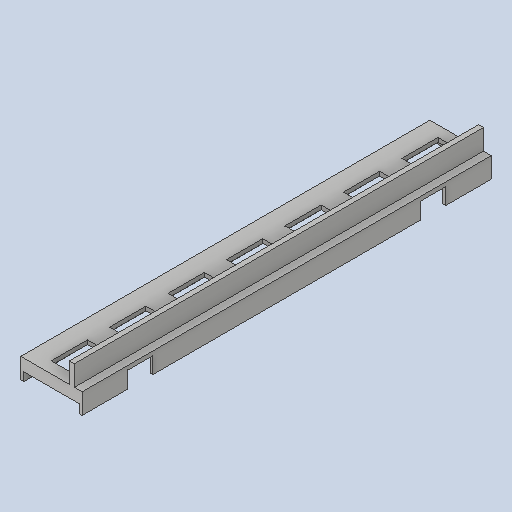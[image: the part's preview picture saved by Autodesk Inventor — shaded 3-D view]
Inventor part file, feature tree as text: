
AUTODESK INVENTOR PART (.ipt)
format: ipt  version: 2023 (Build 270158000, 158)  size: 224,768 bytes
history: native  units: mm
features: other x56, extrude x11, sketch x11
ambient origin geometry x8: Origin, YZ Plane, XZ Plane, XY Plane, X Axis, Y Axis, Z Axis, Center Point
bodies: Solid1 (feature_tree)
feature tree (78):
  extrude  "Extrusion1"  Depth=250.0mm TaperAngle=0.0deg
  extrude  "Extrusion2"  Depth=8.0mm TaperAngle=0.0deg
  extrude  "Extrusion3"  Depth=8.0mm TaperAngle=0.0deg
  extrude  "Extrusion4"  Depth=8.0mm TaperAngle=0.0deg
  extrude  "Extrusion5"  Depth=37.5mm TaperAngle=0.0deg
  extrude  "Extrusion6"  TaperAngle=0.0deg  [1 undecoded]
  extrude  "Extrusion7"  [1 undecoded]
  extrude  "Extrusion8"  [1 undecoded]
  extrude  "Extrusion9"  [1 undecoded]
  extrude  "Extrusion10"  [1 undecoded]
  extrude  "Extrusion11"  [1 undecoded]
  other  "p_XY"
  other  "p_YZ"
  other  "p_ZX"
  other  "p_X"
  other  "p_Y"
  other  "p_Z"
  other  "p_Center"
  other  "p1_XY"
  other  "p1_YZ"
  other  "p1_ZX"
  other  "p1_X"
  other  "p1_Y"
  other  "p1_Z"
  other  "p1_Center"
  other  "p2_XY"
  other  "p2_YZ"
  other  "p2_ZX"
  other  "p2_X"
  other  "p2_Y"
  other  "p2_Z"
  other  "p2_Center"
  other  "p3_XY"
  other  "p3_YZ"
  other  "p3_ZX"
  other  "p3_X"
  other  "p3_Y"
  other  "p3_Z"
  other  "p3_Center"
  other  "p4_XY"
  other  "p4_YZ"
  other  "p4_ZX"
  other  "p4_X"
  other  "p4_Y"
  other  "p4_Z"
  other  "p4_Center"
  other  "p5_XY"
  other  "p5_YZ"
  other  "p5_ZX"
  other  "p5_X"
  other  "p5_Y"
  other  "p5_Z"
  other  "p5_Center"
  other  "p6_XY"
  other  "p6_YZ"
  other  "p6_ZX"
  other  "p6_X"
  other  "p6_Y"
  other  "p6_Z"
  other  "p6_Center"
  other  "p7_XY"
  other  "p7_YZ"
  other  "p7_ZX"
  other  "p7_X"
  other  "p7_Y"
  other  "p7_Z"
  other  "p7_Center"
  sketch  "Sketch_1"  dims[d0=250.0mm d1=0.0mm d2=8.0mm d3=0.0mm]
  sketch  "Sketch_2"  dims[d4=8.0mm d5=0.0mm d6=8.0mm d7=0.0mm]
  sketch  "Sketch_3"  dims[d8=8.0mm d9=0.0mm d10=8.0mm d11=0.0mm]
  sketch  "Sketch_4"  dims[d12=8.0mm d13=0.0mm d14=8.0mm d15=0.0mm]
  sketch  "Sketch_5"  dims[d16=37.5mm d17=0.0mm d18=37.5mm d19=0.0mm]
  sketch  "Sketch_6"  dims[d20=4.7mm d21=0.0mm d22=0.0mm]
  sketch  "Sketch_7"
  sketch  "Sketch_8"
  sketch  "Sketch_10"
  sketch  "Sketch_11"
  sketch  "Sketch_13"
note: 6 required parameter values undecoded (feature->parameter linkage not recoverable at this tier; creation-order binding heuristic only, values carry confidence <= 0.55)
